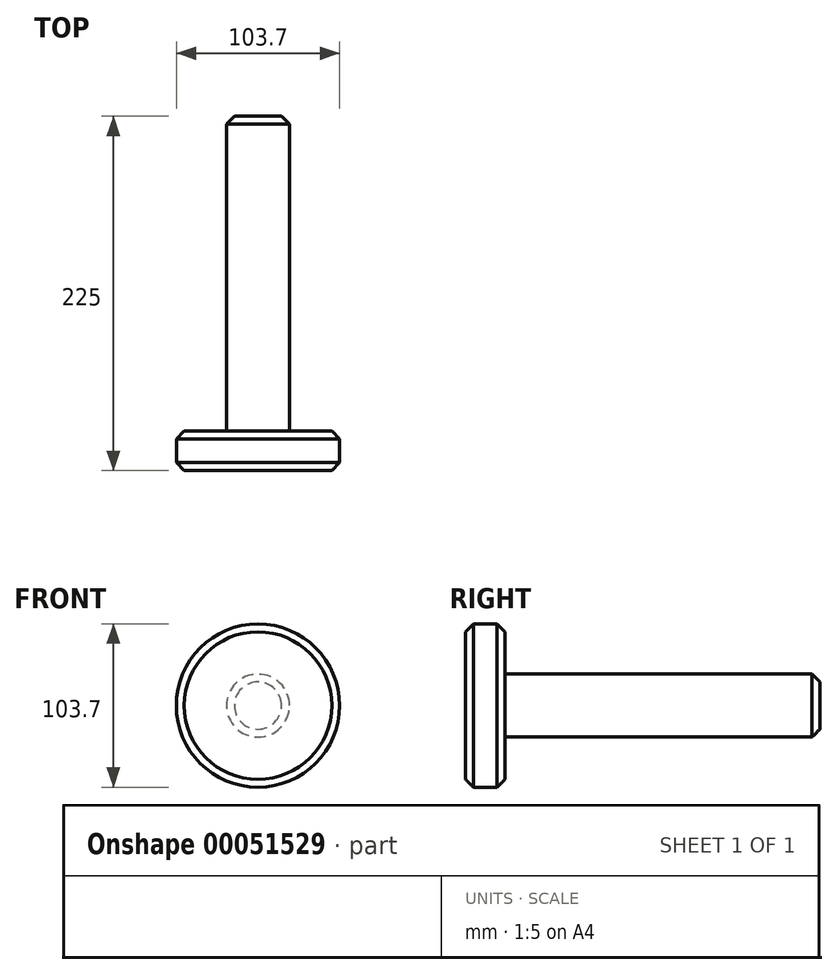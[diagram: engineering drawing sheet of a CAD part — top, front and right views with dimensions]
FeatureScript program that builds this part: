
annotation { "Feature Type Name" : "Feature", "Feature Type Description" : "" }
export const myFeature = defineFeature(function(context is Context, id is Id, definition is map)
    precondition{}
    {
        {
            var Q0;
            Q0=qCreatedBy(makeId("Front.planeOp"),FACE);
            var sketch = newSketch(context, id + "F0", { "sketchPlane" : qUnion([Q0])});
            skCircle(sketch, "E0", {"center": v(0, 0) * mm, "radius": 20 * mm});
            skSolve(sketch);
        }
        {
            var Q0;
            Q0=makeQuery(id+"F0.imprint","IMPRINT",FACE,{"disambiguationData":[TD([[makeQuery(id+"F0.imprint","IMPRINT",EDGE,{"derivedFrom":sQuery(id+"F0.wireOp",EDGE,"E0")}),1.0]])]});
            extrude(context, id + "F1", {"entities" : qUnion([Q0]), "depth" : 200 * mm});
        }
        {
            var Q0;
            Q0=makeQuery(id+"F1.opExtrude","CAP_FACE",FACE,{"disambiguationData":[OSD([sQuery(id+"F0.wireOp",EDGE,"E0")])],"isStart":false});
            var sketch = newSketch(context, id + "F2", { "sketchPlane" : qUnion([Q0])});
            skCircle(sketch, "E1", {"center": v(0, 0) * mm, "radius": 51.85 * mm});
            skSolve(sketch);
        }
        {
            var Q0;
            Q0 = qSketchRegion(id + "F2", true);
            var Q1;
            Q1=makeQuery(id+"F2.imprint","IMPRINT",FACE,{"disambiguationData":[TD([[makeQuery(id+"F2.imprint","IMPRINT",EDGE,{"derivedFrom":sQuery(id+"F2.wireOp",EDGE,"E1")}),1.0]])]});
            extrude(context, id + "F3", {"entities" : qUnion([Q0, Q1]), "operationType" : NewBodyOperationType.ADD, "depth" : 25 * mm});
        }
        {
            var Q0;
            Q0=makeQuery(id+"F3.opExtrude","CAP_EDGE",EDGE,{"disambiguationData":[OSD([sQuery(id+"F2.wireOp",EDGE,"E1")])],"isStart":false});
            var Q1;
            Q1=makeQuery(id+"F3.opExtrude","CAP_EDGE",EDGE,{"disambiguationData":[OSD([sQuery(id+"F2.wireOp",EDGE,"E1")])],"isStart":true});
            var Q2;
            Q2=makeQuery(id+"F1.opExtrude","CAP_EDGE",EDGE,{"disambiguationData":[OSD([sQuery(id+"F0.wireOp",EDGE,"E0")])],"isStart":true});
            chamfer(context, id + "F4", {"entities" : qUnion([Q0, Q1, Q2]), "width" : 5 * mm, "tangentPropagation" : true});
        }
        {
            var Q0;
            Q0=qCreatedBy(makeId("Top.planeOp"),FACE);
            var sketch = newSketch(context, id + "F5", { "sketchPlane" : qUnion([Q0])});
            skCircle(sketch, "E2", {"center": v(0, -18.58) * mm, "radius": 7.2 * mm});
            skSolve(sketch);
        }
        {
            var Q0;
            Q0 = qSketchRegion(id + "F5", true);
            extrude(context, id + "F6", {"entities" : qUnion([Q0]), "operationType" : NewBodyOperationType.REMOVE, "endBound" : BoundingType.THROUGH_ALL, "oppositeDirection" : true, "depth" : 25 * mm, "hasSecondDirection" : true, "secondDirectionOppositeDirection" : true, "secondDirectionDepth" : 25 * mm});
        }
    });
